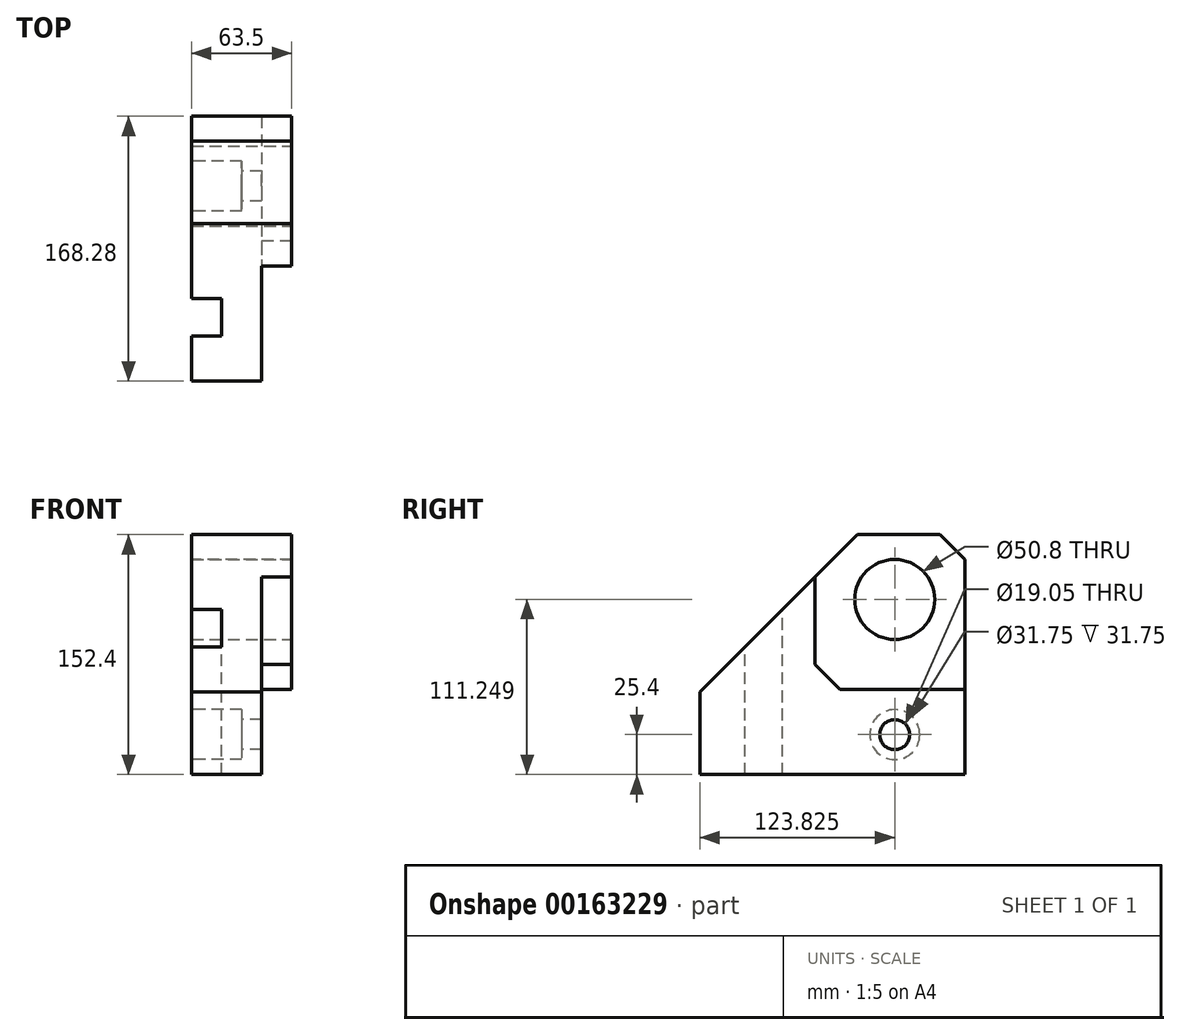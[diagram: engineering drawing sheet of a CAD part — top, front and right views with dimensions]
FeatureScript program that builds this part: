
annotation { "Feature Type Name" : "Feature", "Feature Type Description" : "" }
export const myFeature = defineFeature(function(context is Context, id is Id, definition is map)
    precondition{}
    {
        {
            var Q0;
            Q0=qCreatedBy(makeId("Right.planeOp"),FACE);
            var sketch = newSketch(context, id + "F0", { "sketchPlane" : qUnion([Q0])});
            skLineSegment(sketch, "E0", {"start": v(0, 0) * mm, "end": v(0, 52.39) * mm});
            skLineSegment(sketch, "E1", {"start": v(0, 52.39) * mm, "end": v(100.01, 152.4) * mm});
            skLineSegment(sketch, "E2", {"start": v(100.01, 152.4) * mm, "end": v(152.4, 152.4) * mm});
            skLineSegment(sketch, "E3", {"start": v(152.4, 152.4) * mm, "end": v(168.28, 136.53) * mm});
            skLineSegment(sketch, "E4", {"start": v(168.28, 136.53) * mm, "end": v(168.28, 0) * mm});
            skLineSegment(sketch, "E5", {"start": v(168.28, 0) * mm, "end": v(0, 0) * mm});
            skSolve(sketch);
        }
        {
            var Q0;
            Q0=makeQuery(id+"F0.imprint","IMPRINT",FACE,{"disambiguationData":[TD([[makeQuery(id+"F0.imprint","IMPRINT",EDGE,{"derivedFrom":sQuery(id+"F0.wireOp",EDGE,"E0")}),-1.0]])]});
            extrude(context, id + "F1", {"entities" : qUnion([Q0]), "depth" : 44.45 * mm});
        }
        {
            var Q0;
            Q0=makeQuery(id+"F1.opExtrude","SWEPT_FACE",FACE,{"disambiguationData":[OSD([sQuery(id+"F0.wireOp",EDGE,"E2")])]});
            var sketch = newSketch(context, id + "F2", { "sketchPlane" : qUnion([Q0])});
            skLineSegment(sketch, "E6.bottom", {"start": v(0, 52.39) * mm, "end": v(19.05, 52.39) * mm});
            skLineSegment(sketch, "E6.top", {"start": v(0, 28.58) * mm, "end": v(19.05, 28.58) * mm});
            skLineSegment(sketch, "E6.left", {"start": v(0, 52.39) * mm, "end": v(0, 28.58) * mm});
            skLineSegment(sketch, "E6.right", {"start": v(19.05, 52.39) * mm, "end": v(19.05, 28.58) * mm});
            skSolve(sketch);
        }
        {
            var Q0;
            Q0=makeQuery(id+"F2.imprint","IMPRINT",FACE,{"disambiguationData":[TD([[makeQuery(id+"F2.imprint","IMPRINT",EDGE,{"derivedFrom":sQuery(id+"F2.wireOp",EDGE,"E6.bottom")}),-1.0]])]});
            extrude(context, id + "F3", {"entities" : qUnion([Q0]), "operationType" : NewBodyOperationType.REMOVE, "endBound" : BoundingType.THROUGH_ALL, "oppositeDirection" : true, "depth" : 25.4 * mm});
        }
        {
            var Q0;
            Q0=makeQuery(id+"F1.opExtrude","CAP_FACE",FACE,{"disambiguationData":[OSD([sQuery(id+"F0.wireOp",EDGE,"E0"),sQuery(id+"F0.wireOp",EDGE,"E1"),sQuery(id+"F0.wireOp",EDGE,"E2"),sQuery(id+"F0.wireOp",EDGE,"E3"),sQuery(id+"F0.wireOp",EDGE,"E4"),sQuery(id+"F0.wireOp",EDGE,"E5")])],"isStart":false});
            var sketch = newSketch(context, id + "F4", { "sketchPlane" : qUnion([Q0])});
            skLineSegment(sketch, "E7", {"start": v(152.4, 152.4) * mm, "end": v(168.28, 136.53) * mm});
            skLineSegment(sketch, "E8", {"start": v(168.28, 136.53) * mm, "end": v(168.28, 54.1) * mm});
            skLineSegment(sketch, "E9", {"start": v(168.28, 54.1) * mm, "end": v(88.9, 54.1) * mm});
            skLineSegment(sketch, "E10", {"start": v(88.9, 54.1) * mm, "end": v(73.02, 69.97) * mm});
            skLineSegment(sketch, "E11", {"start": v(73.02, 69.97) * mm, "end": v(73.02, 125.41) * mm});
            skLineSegment(sketch, "E12", {"start": v(73.03, 125.41) * mm, "end": v(100.01, 152.4) * mm});
            skLineSegment(sketch, "E13", {"start": v(100.01, 152.4) * mm, "end": v(152.4, 152.4) * mm});
            skPoint(sketch, "E14", {"position": v(123.83, 111.25) * mm});
            skSolve(sketch);
        }
        {
            var Q0;
            Q0=makeQuery(id+"F4.imprint","IMPRINT",FACE,{"disambiguationData":[TD([[makeQuery(id+"F4.imprint","IMPRINT",EDGE,{"derivedFrom":sQuery(id+"F4.wireOp",EDGE,"E7")}),-1.0]])]});
            extrude(context, id + "F5", {"entities" : qUnion([Q0]), "operationType" : NewBodyOperationType.ADD, "depth" : 19.05 * mm});
        }
        {
            var Q0;
            Q0=sQuery(id+"F4.wireOp",VERTEX,"E14");
            var Q1;
            Q1=makeQuery(id+"F1.opExtrude","SWEPT_BODY",BODY,{"disambiguationData":[OSD([sQuery(id+"F0.wireOp",EDGE,"E0"),sQuery(id+"F0.wireOp",EDGE,"E1"),sQuery(id+"F0.wireOp",EDGE,"E2"),sQuery(id+"F0.wireOp",EDGE,"E3"),sQuery(id+"F0.wireOp",EDGE,"E4"),sQuery(id+"F0.wireOp",EDGE,"E5")])]});
            hole(context, id + "F6", {"style" : HoleStyle.SIMPLE, "endStyle" : HoleEndStyle.THROUGH, "holeDiameter" : 50.8 * mm, "locations" : qUnion([Q0]), "scope" : qUnion([Q1]), "isTappedThrough" : true});
        }
        {
            var Q0;
            Q0=sQuery(id+"F4.wireOp",VERTEX,"E14");
            var Q1;
            Q1=makeQuery(id+"F1.opExtrude","SWEPT_BODY",BODY,{"disambiguationData":[OSD([sQuery(id+"F0.wireOp",EDGE,"E0"),sQuery(id+"F0.wireOp",EDGE,"E1"),sQuery(id+"F0.wireOp",EDGE,"E2"),sQuery(id+"F0.wireOp",EDGE,"E3"),sQuery(id+"F0.wireOp",EDGE,"E4"),sQuery(id+"F0.wireOp",EDGE,"E5")])]});
            hole(context, id + "F7", {"style" : HoleStyle.SIMPLE, "endStyle" : HoleEndStyle.THROUGH, "oppositeDirection" : true, "holeDiameter" : 50.8 * mm, "locations" : qUnion([Q0]), "scope" : qUnion([Q1]), "isTappedThrough" : true});
        }
        {
            var Q0;
            {var subQ0=sQuery(id+"F0.wireOp",EDGE,"E4");var subQ1=sQuery(id+"F0.wireOp",EDGE,"E3");var subQ2=sQuery(id+"F0.wireOp",EDGE,"E2");var subQ3=sQuery(id+"F0.wireOp",EDGE,"E1");var subQ4=sQuery(id+"F0.wireOp",EDGE,"E5");Q0=makeQuery(id+"F3.boolean.opBoolean","SPLIT",FACE,{"disambiguationData":[TD([makeQuery(id+"F1.opExtrude","SWEPT_FACE",FACE,{"disambiguationData":[OSD([subQ2])]})])],"derivedFrom":makeQuery(id+"F1.opExtrude","CAP_FACE",FACE,{"disambiguationData":[OSD([sQuery(id+"F0.wireOp",EDGE,"E0"),subQ3,subQ2,subQ1,subQ0,subQ4])],"isStart":true})});}
            var sketch = newSketch(context, id + "F8", { "sketchPlane" : qUnion([Q0])});
            skPoint(sketch, "E15", {"position": v(-123.83, 25.4) * mm});
            skSolve(sketch);
        }
        {
            var Q0;
            Q0=sQuery(id+"F8.wireOp",VERTEX,"E15");
            var Q1;
            Q1=makeQuery(id+"F1.opExtrude","SWEPT_BODY",BODY,{"disambiguationData":[OSD([sQuery(id+"F0.wireOp",EDGE,"E0"),sQuery(id+"F0.wireOp",EDGE,"E1"),sQuery(id+"F0.wireOp",EDGE,"E2"),sQuery(id+"F0.wireOp",EDGE,"E3"),sQuery(id+"F0.wireOp",EDGE,"E4"),sQuery(id+"F0.wireOp",EDGE,"E5")])]});
            hole(context, id + "F9", {"style" : HoleStyle.C_BORE, "endStyle" : HoleEndStyle.THROUGH, "holeDiameter" : 19.05 * mm, "cBoreDiameter" : 31.75 * mm, "cBoreDepth" : 31.75 * mm, "locations" : qUnion([Q0]), "scope" : qUnion([Q1]), "isTappedThrough" : true});
        }
    });
